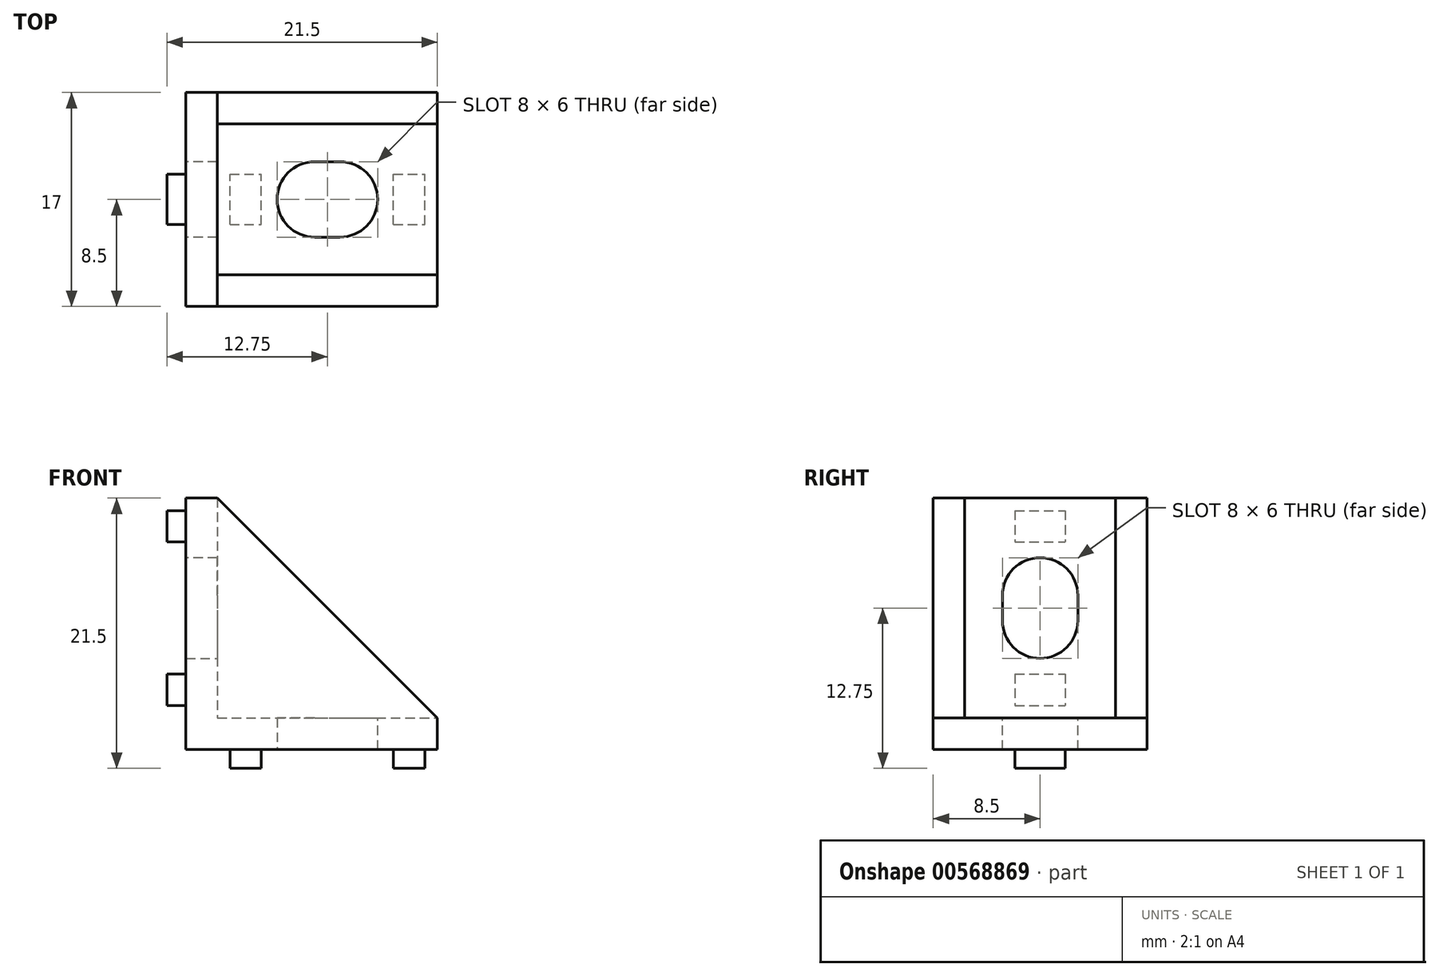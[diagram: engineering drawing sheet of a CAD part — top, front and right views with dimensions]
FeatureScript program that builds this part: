
annotation { "Feature Type Name" : "Feature", "Feature Type Description" : "" }
export const myFeature = defineFeature(function(context is Context, id is Id, definition is map)
    precondition{}
    {
        {
            var Q0;
            Q0=qCreatedBy(makeId("Front.planeOp"),FACE);
            var sketch = newSketch(context, id + "F0", { "sketchPlane" : qUnion([Q0])});
            skLineSegment(sketch, "E0", {"start": v(0, 20) * mm, "end": v(0, 0) * mm});
            skLineSegment(sketch, "E1", {"start": v(0, 0) * mm, "end": v(20, 0) * mm});
            skLineSegment(sketch, "E2", {"start": v(20, 0) * mm, "end": v(20, 2.5) * mm});
            skLineSegment(sketch, "E3", {"start": v(20, 2.5) * mm, "end": v(2.5, 20) * mm});
            skLineSegment(sketch, "E4", {"start": v(2.5, 20) * mm, "end": v(0, 20) * mm});
            skLineSegment(sketch, "E5", {"start": v(2.5, 20) * mm, "end": v(2.5, 2.5) * mm});
            skLineSegment(sketch, "E6", {"start": v(2.5, 2.5) * mm, "end": v(20, 2.5) * mm});
            skLineSegment(sketch, "E7", {"start": v(3.5, 0) * mm, "end": v(3.5, -1.5) * mm});
            skLineSegment(sketch, "E8", {"start": v(3.5, -1.5) * mm, "end": v(6, -1.5) * mm});
            skLineSegment(sketch, "E9", {"start": v(6, -1.5) * mm, "end": v(6, 0) * mm});
            skLineSegment(sketch, "E10", {"start": v(19, 0) * mm, "end": v(19, -1.5) * mm});
            skLineSegment(sketch, "E11", {"start": v(19, -1.5) * mm, "end": v(16.5, -1.5) * mm});
            skLineSegment(sketch, "E12", {"start": v(16.5, -1.5) * mm, "end": v(16.5, 0) * mm});
            skLineSegment(sketch, "E13", {"start": v(0, 3.5) * mm, "end": v(-1.5, 3.5) * mm});
            skLineSegment(sketch, "E14", {"start": v(-1.5, 3.5) * mm, "end": v(-1.5, 6) * mm});
            skLineSegment(sketch, "E15", {"start": v(-1.5, 6) * mm, "end": v(0, 6) * mm});
            skLineSegment(sketch, "E16", {"start": v(0, 16.5) * mm, "end": v(-1.5, 16.5) * mm});
            skLineSegment(sketch, "E17", {"start": v(-1.5, 16.5) * mm, "end": v(-1.5, 19) * mm});
            skLineSegment(sketch, "E18", {"start": v(-1.5, 19) * mm, "end": v(0, 19) * mm});
            skLineSegment(sketch, "E19", {"start": v(-1.5, 16.5) * mm, "end": v(-1.5, 6) * mm, "construction": true});
            skLineSegment(sketch, "E20", {"start": v(6, -1.5) * mm, "end": v(16.5, -1.5) * mm, "construction": true});
            skLineSegment(sketch, "E21", {"start": v(0, 7.25) * mm, "end": v(2.5, 7.25) * mm});
            skLineSegment(sketch, "E22", {"start": v(2.5, 15.25) * mm, "end": v(0, 15.25) * mm});
            skPoint(sketch, "E23", {"position": v(0, 11.25) * mm});
            skPoint(sketch, "E24", {"position": v(11.25, 0) * mm});
            skLineSegment(sketch, "E25", {"start": v(7.25, 0) * mm, "end": v(7.25, 2.5) * mm});
            skLineSegment(sketch, "E26", {"start": v(15.25, 0) * mm, "end": v(15.25, 2.5) * mm});
            skSolve(sketch);
        }
        {
            var Q0;
            Q0=makeQuery(id+"F0.imprint","IMPRINT",FACE,{"disambiguationData":[TD([[makeQuery(id+"F0.imprint","IMPRINT",EDGE,{"derivedFrom":sQuery(id+"F0.wireOp",EDGE,"E3")}),1.0]])]});
            var Q1;
            {var subQ0=sQuery(id+"F0.wireOp",EDGE,"E2");Q1=makeQuery(id+"F0.imprint","IMPRINT",FACE,{"disambiguationData":[TD([[makeQuery(id+"F0.imprint","IMPRINT",EDGE,{"derivedFrom":subQ0}),1.0]])]});}
            var Q2;
            {var subQ3=sQuery(id+"F0.wireOp",EDGE,"E4");Q2=makeQuery(id+"F0.imprint","IMPRINT",FACE,{"disambiguationData":[TD([[makeQuery(id+"F0.imprint","IMPRINT",EDGE,{"derivedFrom":subQ3}),1.0]])]});}
            var Q3;
            {var subQ6=sQuery(id+"F0.wireOp",EDGE,"E21");Q3=makeQuery(id+"F0.imprint","IMPRINT",FACE,{"disambiguationData":[TD([[makeQuery(id+"F0.imprint","IMPRINT",EDGE,{"derivedFrom":subQ6}),-1.0]])]});}
            var Q4;
            {var subQ0=sQuery(id+"F0.wireOp",EDGE,"E21");Q4=makeQuery(id+"F0.imprint","IMPRINT",FACE,{"disambiguationData":[TD([[makeQuery(id+"F0.imprint","IMPRINT",EDGE,{"derivedFrom":subQ0}),1.0]])]});}
            var Q5;
            {var subQ0=sQuery(id+"F0.wireOp",EDGE,"E25");Q5=makeQuery(id+"F0.imprint","IMPRINT",FACE,{"disambiguationData":[TD([[makeQuery(id+"F0.imprint","IMPRINT",EDGE,{"derivedFrom":subQ0}),-1.0]])]});}
            extrude(context, id + "F1", {"entities" : qUnion([Q0, Q1, Q2, Q3, Q4, Q5]), "depth" : 17 * mm, "offsetDistance" : 25 * mm});
        }
        {
            var Q0;
            Q0=makeQuery(id+"F0.imprint","IMPRINT",FACE,{"disambiguationData":[TD([[makeQuery(id+"F0.imprint","IMPRINT",EDGE,{"derivedFrom":sQuery(id+"F0.wireOp",EDGE,"E3")}),1.0]])]});
            extrude(context, id + "F2", {"entities" : qUnion([Q0]), "operationType" : NewBodyOperationType.REMOVE, "depth" : 14.5 * mm, "offsetDistance" : 25 * mm, "hasSecondDirection" : true, "secondDirectionOppositeDirection" : false, "secondDirectionDepth" : 2.5 * mm});
        }
        {
            var Q0;
            {var subQ0=sQuery(id+"F0.wireOp",EDGE,"E21");Q0=makeQuery(id+"F0.imprint","IMPRINT",FACE,{"disambiguationData":[TD([[makeQuery(id+"F0.imprint","IMPRINT",EDGE,{"derivedFrom":subQ0}),1.0]])]});}
            var Q1;
            {var subQ0=sQuery(id+"F0.wireOp",EDGE,"E25");Q1=makeQuery(id+"F0.imprint","IMPRINT",FACE,{"disambiguationData":[TD([[makeQuery(id+"F0.imprint","IMPRINT",EDGE,{"derivedFrom":subQ0}),-1.0]])]});}
            extrude(context, id + "F3", {"entities" : qUnion([Q0, Q1]), "operationType" : NewBodyOperationType.REMOVE, "depth" : 11.5 * mm, "offsetDistance" : 25 * mm, "hasSecondDirection" : true, "secondDirectionOppositeDirection" : false, "secondDirectionDepth" : 5.5 * mm});
        }
        {
            var Q0;
            Q0=makeQuery(id+"F3.boolean.opBoolean","COPY",EDGE,{"derivedFrom":makeQuery(id+"F3.opExtrude","CAP_EDGE",EDGE,{"disambiguationData":[OSD([sQuery(id+"F0.wireOp",EDGE,"E21")])],"isStart":false})});
            var Q1;
            Q1=makeQuery(id+"F3.boolean.opBoolean","COPY",EDGE,{"derivedFrom":makeQuery(id+"F3.opExtrude","CAP_EDGE",EDGE,{"disambiguationData":[OSD([sQuery(id+"F0.wireOp",EDGE,"E21")])],"isStart":true})});
            var Q2;
            Q2=makeQuery(id+"F3.boolean.opBoolean","COPY",EDGE,{"derivedFrom":makeQuery(id+"F3.opExtrude","CAP_EDGE",EDGE,{"disambiguationData":[OSD([sQuery(id+"F0.wireOp",EDGE,"E22")])],"isStart":false})});
            var Q3;
            Q3=makeQuery(id+"F3.boolean.opBoolean","COPY",EDGE,{"derivedFrom":makeQuery(id+"F3.opExtrude","CAP_EDGE",EDGE,{"disambiguationData":[OSD([sQuery(id+"F0.wireOp",EDGE,"E22")])],"isStart":true})});
            var Q4;
            Q4=makeQuery(id+"F3.boolean.opBoolean","COPY",EDGE,{"derivedFrom":makeQuery(id+"F3.opExtrude","CAP_EDGE",EDGE,{"disambiguationData":[OSD([sQuery(id+"F0.wireOp",EDGE,"E25")])],"isStart":false})});
            var Q5;
            Q5=makeQuery(id+"F3.boolean.opBoolean","COPY",EDGE,{"derivedFrom":makeQuery(id+"F3.opExtrude","CAP_EDGE",EDGE,{"disambiguationData":[OSD([sQuery(id+"F0.wireOp",EDGE,"E25")])],"isStart":true})});
            var Q6;
            Q6=makeQuery(id+"F3.boolean.opBoolean","COPY",EDGE,{"derivedFrom":makeQuery(id+"F3.opExtrude","CAP_EDGE",EDGE,{"disambiguationData":[OSD([sQuery(id+"F0.wireOp",EDGE,"E26")])],"isStart":false})});
            var Q7;
            Q7=makeQuery(id+"F3.boolean.opBoolean","COPY",EDGE,{"derivedFrom":makeQuery(id+"F3.opExtrude","CAP_EDGE",EDGE,{"disambiguationData":[OSD([sQuery(id+"F0.wireOp",EDGE,"E26")])],"isStart":true})});
            fillet(context, id + "F4", {"entities" : qUnion([Q0, Q1, Q2, Q3, Q4, Q5, Q6, Q7]), "radius" : 3 * mm, "tangentPropagation" : true, "allowEdgeOverflow" : false});
        }
        {
            var Q0;
            {var subQ0=sQuery(id+"F0.wireOp",EDGE,"E16");Q0=makeQuery(id+"F0.imprint","IMPRINT",FACE,{"disambiguationData":[TD([[makeQuery(id+"F0.imprint","IMPRINT",EDGE,{"derivedFrom":subQ0}),-1.0]])]});}
            var Q1;
            {var subQ0=sQuery(id+"F0.wireOp",EDGE,"E13");Q1=makeQuery(id+"F0.imprint","IMPRINT",FACE,{"disambiguationData":[TD([[makeQuery(id+"F0.imprint","IMPRINT",EDGE,{"derivedFrom":subQ0}),-1.0]])]});}
            var Q2;
            {var subQ0=sQuery(id+"F0.wireOp",EDGE,"E7");Q2=makeQuery(id+"F0.imprint","IMPRINT",FACE,{"disambiguationData":[TD([[makeQuery(id+"F0.imprint","IMPRINT",EDGE,{"derivedFrom":subQ0}),1.0]])]});}
            var Q3;
            {var subQ0=sQuery(id+"F0.wireOp",EDGE,"E10");Q3=makeQuery(id+"F0.imprint","IMPRINT",FACE,{"disambiguationData":[TD([[makeQuery(id+"F0.imprint","IMPRINT",EDGE,{"derivedFrom":subQ0}),-1.0]])]});}
            extrude(context, id + "F5", {"entities" : qUnion([Q0, Q1, Q2, Q3]), "operationType" : NewBodyOperationType.ADD, "depth" : 10.5 * mm, "offsetDistance" : 25 * mm, "hasSecondDirection" : true, "secondDirectionOppositeDirection" : false, "secondDirectionDepth" : 6.5 * mm});
        }
    });
